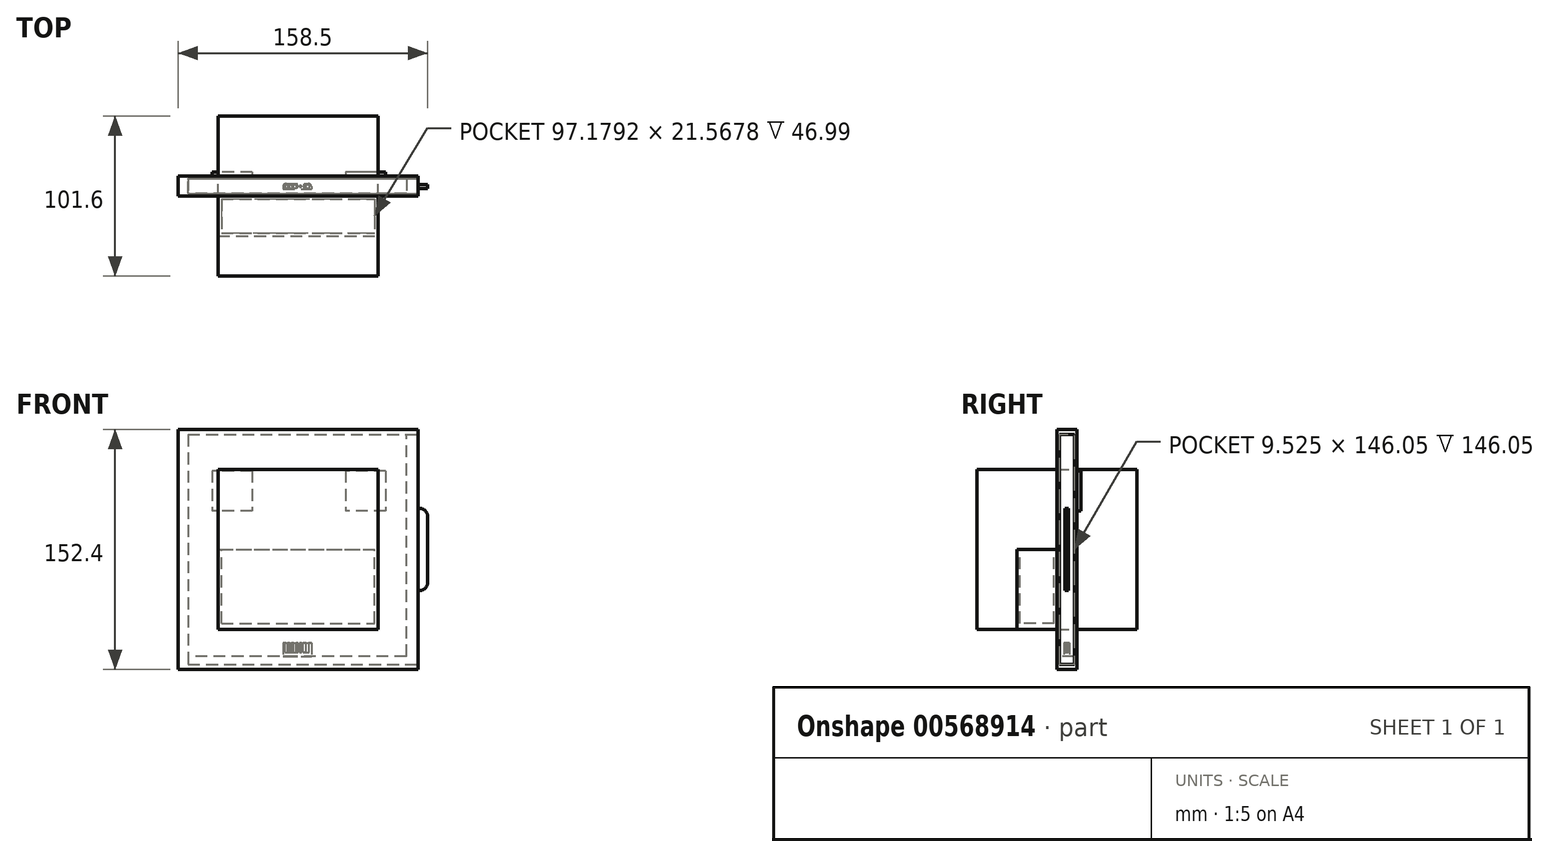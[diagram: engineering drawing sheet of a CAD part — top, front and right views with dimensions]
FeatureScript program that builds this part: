
annotation { "Feature Type Name" : "Feature", "Feature Type Description" : "" }
export const myFeature = defineFeature(function(context is Context, id is Id, definition is map)
    precondition{}
    {
        {
            var Q0;
            Q0=qCreatedBy(makeId("Front.planeOp"),FACE);
            var sketch = newSketch(context, id + "F0", { "sketchPlane" : qUnion([Q0])});
            skLineSegment(sketch, "E0.bottom", {"start": v(-34.8, 71.2) * mm, "end": v(34.8, 71.2) * mm});
            skLineSegment(sketch, "E0.top", {"start": v(-34.8, -71.2) * mm, "end": v(34.8, -71.2) * mm});
            skLineSegment(sketch, "E0.left", {"start": v(-34.8, 71.2) * mm, "end": v(-34.8, -71.2) * mm});
            skLineSegment(sketch, "E0.right", {"start": v(34.8, 71.2) * mm, "end": v(34.8, -71.2) * mm});
            skPoint(sketch, "E0.middle", {"position": v(0, 0) * mm});
            skSolve(sketch);
        }
        {
            var Q0;
            Q0=qCreatedBy(makeId("Front.planeOp"),FACE);
            var sketch = newSketch(context, id + "F1", { "sketchPlane" : qUnion([Q0])});
            skLineSegment(sketch, "E1.bottom", {"start": v(-76.2, 76.2) * mm, "end": v(76.2, 76.2) * mm});
            skLineSegment(sketch, "E1.top", {"start": v(-76.2, -76.2) * mm, "end": v(76.2, -76.2) * mm});
            skLineSegment(sketch, "E1.left", {"start": v(-76.2, 76.2) * mm, "end": v(-76.2, -76.2) * mm});
            skLineSegment(sketch, "E1.right", {"start": v(76.2, 76.2) * mm, "end": v(76.2, -76.2) * mm});
            skPoint(sketch, "E1.middle", {"position": v(0, 0) * mm});
            skSolve(sketch);
        }
        {
            var Q0;
            Q0=makeQuery(id+"F1.imprint","IMPRINT",FACE,{"disambiguationData":[TD([[makeQuery(id+"F1.imprint","IMPRINT",EDGE,{"derivedFrom":sQuery(id+"F1.wireOp",EDGE,"E1.bottom")}),-1.0]])]});
            extrude(context, id + "F2", {"entities" : qUnion([Q0]), "oppositeDirection" : true, "depth" : 12.7 * mm, "offsetDistance" : 25.4 * mm});
        }
        {
            var Q0;
            Q0=makeQuery(id+"F2.opExtrude","CAP_FACE",FACE,{"disambiguationData":[OSD([sQuery(id+"F1.wireOp",EDGE,"E1.bottom"),sQuery(id+"F1.wireOp",EDGE,"E1.top"),sQuery(id+"F1.wireOp",EDGE,"E1.left"),sQuery(id+"F1.wireOp",EDGE,"E1.right")])],"isStart":false});
            var sketch = newSketch(context, id + "F3", { "sketchPlane" : qUnion([Q0])});
            skLineSegment(sketch, "E2.bottom", {"start": v(-55.75, 49.94) * mm, "end": v(-30.35, 49.94) * mm});
            skLineSegment(sketch, "E2.top", {"start": v(-55.75, 24.54) * mm, "end": v(-30.35, 24.54) * mm});
            skLineSegment(sketch, "E2.left", {"start": v(-55.75, 49.94) * mm, "end": v(-55.75, 24.54) * mm});
            skLineSegment(sketch, "E2.right", {"start": v(-30.35, 49.94) * mm, "end": v(-30.35, 24.54) * mm});
            skPoint(sketch, "E2.middle", {"position": v(-43.05, 37.24) * mm});
            skLineSegment(sketch, "E3.bottom", {"start": v(29.1, 49.94) * mm, "end": v(54.5, 49.94) * mm});
            skLineSegment(sketch, "E3.top", {"start": v(29.1, 24.54) * mm, "end": v(54.5, 24.54) * mm});
            skLineSegment(sketch, "E3.left", {"start": v(29.1, 49.94) * mm, "end": v(29.1, 24.54) * mm});
            skLineSegment(sketch, "E3.right", {"start": v(54.5, 49.94) * mm, "end": v(54.5, 24.54) * mm});
            skPoint(sketch, "E3.middle", {"position": v(41.8, 37.24) * mm});
            skSolve(sketch);
        }
        {
            var Q0;
            Q0=makeQuery(id+"F3.imprint","IMPRINT",FACE,{"disambiguationData":[TD([[makeQuery(id+"F3.imprint","IMPRINT",EDGE,{"derivedFrom":sQuery(id+"F3.wireOp",EDGE,"E2.bottom")}),-1.0]])]});
            var Q1;
            Q1=makeQuery(id+"F3.imprint","IMPRINT",FACE,{"disambiguationData":[TD([[makeQuery(id+"F3.imprint","IMPRINT",EDGE,{"derivedFrom":sQuery(id+"F3.wireOp",EDGE,"E3.bottom")}),-1.0]])]});
            extrude(context, id + "F4", {"entities" : qUnion([Q0, Q1]), "operationType" : NewBodyOperationType.ADD, "depth" : 2.54 * mm, "offsetDistance" : 25.4 * mm});
        }
        {
            var Q0;
            Q0=makeQuery(id+"F2.opExtrude","SWEPT_FACE",FACE,{"disambiguationData":[OSD([sQuery(id+"F1.wireOp",EDGE,"E1.right")])]});
            var sketch = newSketch(context, id + "F5", { "sketchPlane" : qUnion([Q0])});
            skLineSegment(sketch, "E4.bottom", {"start": v(2.4, 71.2) * mm, "end": v(10.3, 71.2) * mm});
            skLineSegment(sketch, "E4.top", {"start": v(2.4, -71.2) * mm, "end": v(10.3, -71.2) * mm});
            skLineSegment(sketch, "E4.left", {"start": v(2.4, 71.2) * mm, "end": v(2.4, -71.2) * mm});
            skLineSegment(sketch, "E4.right", {"start": v(10.3, 71.2) * mm, "end": v(10.3, -71.2) * mm});
            skPoint(sketch, "E4.middle", {"position": v(6.35, 0) * mm});
            skPoint(sketch, "E4.middle.positionSnap0", {"position": v(12.7, 0) * mm});
            skPoint(sketch, "E4.centerSnap0", {"position": v(12.7, 0) * mm});
            skSolve(sketch);
        }
        {
            var Q0;
            Q0=makeQuery(id+"F5.imprint","IMPRINT",FACE,{"disambiguationData":[TD([[makeQuery(id+"F5.imprint","IMPRINT",EDGE,{"derivedFrom":sQuery(id+"F5.wireOp",EDGE,"E4.bottom")}),1.0]])]});
            var sketch = newSketch(context, id + "F6", { "sketchPlane" : qUnion([Q0])});
            skLineSegment(sketch, "E5.bottom", {"start": v(1.59, 73.03) * mm, "end": v(11.11, 73.03) * mm});
            skLineSegment(sketch, "E5.top", {"start": v(1.59, -73.03) * mm, "end": v(11.11, -73.03) * mm});
            skLineSegment(sketch, "E5.left", {"start": v(1.59, 73.03) * mm, "end": v(1.59, -73.03) * mm});
            skLineSegment(sketch, "E5.right", {"start": v(11.11, 73.03) * mm, "end": v(11.11, -73.03) * mm});
            skPoint(sketch, "E5.middle", {"position": v(6.35, 0) * mm});
            skSolve(sketch);
        }
        {
            var Q0;
            Q0=makeQuery(id+"F6.imprint","IMPRINT",FACE,{"disambiguationData":[TD([[makeQuery(id+"F6.imprint","IMPRINT",EDGE,{"derivedFrom":sQuery(id+"F6.wireOp",EDGE,"E5.bottom")}),-1.0]])]});
            var Q1;
            Q1=makeQuery(id+"F6.imprint","IMPRINT",FACE,{"disambiguationData":[TD([[makeQuery(id+"F6.imprint","IMPRINT",EDGE,{"derivedFrom":makeQuery(id+"F5.imprint","IMPRINT",EDGE,{"derivedFrom":sQuery(id+"F5.wireOp",EDGE,"E4.bottom")})}),-1.0]])]});
            extrude(context, id + "F7", {"entities" : qUnion([Q0, Q1]), "operationType" : NewBodyOperationType.REMOVE, "oppositeDirection" : true, "depth" : 146.05 * mm, "offsetDistance" : 25.4 * mm});
        }
        {
            var Q0;
            Q0=makeQuery(id+"F2.opExtrude","CAP_FACE",FACE,{"disambiguationData":[OSD([sQuery(id+"F1.wireOp",EDGE,"E1.bottom"),sQuery(id+"F1.wireOp",EDGE,"E1.top"),sQuery(id+"F1.wireOp",EDGE,"E1.left"),sQuery(id+"F1.wireOp",EDGE,"E1.right")])],"isStart":true});
            var sketch = newSketch(context, id + "F8", { "sketchPlane" : qUnion([Q0])});
            skLineSegment(sketch, "E6.bottom", {"start": v(-50.8, 50.8) * mm, "end": v(50.8, 50.8) * mm});
            skLineSegment(sketch, "E6.top", {"start": v(-50.8, -50.8) * mm, "end": v(50.8, -50.8) * mm});
            skLineSegment(sketch, "E6.left", {"start": v(-50.8, 50.8) * mm, "end": v(-50.8, -50.8) * mm});
            skLineSegment(sketch, "E6.right", {"start": v(50.8, 50.8) * mm, "end": v(50.8, -50.8) * mm});
            skPoint(sketch, "E6.middle", {"position": v(0, 0) * mm});
            skLineSegment(sketch, "E7", {"start": v(-50.8, 0) * mm, "end": v(50.8, 0) * mm});
            skSolve(sketch);
        }
        {
            var Q0;
            {var subQ0=sQuery(id+"F8.wireOp",EDGE,"E6.top");Q0=makeQuery(id+"F8.imprint","IMPRINT",FACE,{"disambiguationData":[TD([[makeQuery(id+"F8.imprint","IMPRINT",EDGE,{"derivedFrom":subQ0}),1.0]])]});}
            extrude(context, id + "F9", {"entities" : qUnion([Q0]), "operationType" : NewBodyOperationType.ADD, "depth" : 25.4 * mm, "offsetDistance" : 25.4 * mm});
        }
        {
            var Q0;
            Q0=makeQuery(id+"F9.opExtrude","SWEPT_FACE",FACE,{"disambiguationData":[OSD([sQuery(id+"F8.wireOp",EDGE,"E7")])]});
            var sketch = newSketch(context, id + "F10", { "sketchPlane" : qUnion([Q0])});
            skLineSegment(sketch, "E8.bottom", {"start": v(-48.59, -1.92) * mm, "end": v(48.59, -1.92) * mm});
            skLineSegment(sketch, "E8.top", {"start": v(-48.59, -23.48) * mm, "end": v(48.59, -23.48) * mm});
            skLineSegment(sketch, "E8.left", {"start": v(-48.59, -1.92) * mm, "end": v(-48.59, -23.48) * mm});
            skLineSegment(sketch, "E8.right", {"start": v(48.59, -1.92) * mm, "end": v(48.59, -23.48) * mm});
            skPoint(sketch, "E8.middle", {"position": v(0, -12.7) * mm});
            skPoint(sketch, "E8.middle.positionSnap0", {"position": v(0, -25.4) * mm});
            skPoint(sketch, "E8.centerSnap0", {"position": v(0, -25.4) * mm});
            skSolve(sketch);
        }
        {
            var Q0;
            Q0=makeQuery(id+"F10.imprint","IMPRINT",FACE,{"disambiguationData":[TD([[makeQuery(id+"F10.imprint","IMPRINT",EDGE,{"derivedFrom":sQuery(id+"F10.wireOp",EDGE,"E8.bottom")}),-1.0]])]});
            extrude(context, id + "F11", {"entities" : qUnion([Q0]), "operationType" : NewBodyOperationType.REMOVE, "oppositeDirection" : true, "depth" : 47 * mm, "offsetDistance" : 25.4 * mm});
        }
        {
            var Q0;
            Q0=makeQuery(id+"F6.imprint","IMPRINT",FACE,{"disambiguationData":[TD([[makeQuery(id+"F6.imprint","IMPRINT",EDGE,{"derivedFrom":sQuery(id+"F6.wireOp",EDGE,"E5.bottom")}),-1.0]])]});
            var Q1;
            Q1=makeQuery(id+"F6.imprint","IMPRINT",FACE,{"disambiguationData":[TD([[makeQuery(id+"F6.imprint","IMPRINT",EDGE,{"derivedFrom":makeQuery(id+"F5.imprint","IMPRINT",EDGE,{"derivedFrom":sQuery(id+"F5.wireOp",EDGE,"E4.bottom")})}),-1.0]])]});
            extrude(context, id + "F12", {"entities" : qUnion([Q0, Q1]), "oppositeDirection" : true, "depth" : 146.05 * mm, "offsetDistance" : 25.4 * mm});
        }
        {
            var Q0;
            Q0=makeQuery(id+"F12.opExtrude","SWEPT_FACE",FACE,{"disambiguationData":[OSD([sQuery(id+"F6.wireOp",EDGE,"E5.left")])]});
            var sketch = newSketch(context, id + "F13", { "sketchPlane" : qUnion([Q0])});
            skLineSegment(sketch, "E9.bottom", {"start": v(68.8, -67.84) * mm, "end": v(-208.5, -67.84) * mm});
            skLineSegment(sketch, "E9.top", {"start": v(68.8, 213.9) * mm, "end": v(-208.5, 213.9) * mm});
            skLineSegment(sketch, "E9.left", {"start": v(68.8, -67.84) * mm, "end": v(68.8, 213.9) * mm});
            skLineSegment(sketch, "E9.right", {"start": v(-208.5, -67.84) * mm, "end": v(-208.5, 213.9) * mm});
            skPoint(sketch, "E9.middle", {"position": v(-69.85, 73.03) * mm});
            skSolve(sketch);
        }
        {
            var Q0;
            {var subQ0=sQuery(id+"F13.wireOp",EDGE,"E9.left");var subQ1=sQuery(id+"F13.wireOp",EDGE,"E9.bottom");var subQ2=makeQuery(id+"F13.imprint","INTERSECT",VERTEX,{"derivedFrom":[subQ1,subQ0]});Q0=makeQuery(id+"F13.imprint","IMPRINT",FACE,{"disambiguationData":[TD([[makeQuery(id+"F13.imprint","IMPRINT",EDGE,{"disambiguationData":[TD([[subQ2,-1.0]])],"derivedFrom":subQ1}),-1.0]])]});}
            extrude(context, id + "F14", {"entities" : qUnion([Q0]), "operationType" : NewBodyOperationType.REMOVE, "oppositeDirection" : true, "depth" : 9.25 * mm, "offsetDistance" : 25.4 * mm});
        }
        {
            var Q0;
            Q0=makeQuery(id+"F14.boolean.opBoolean","COPY",FACE,{"derivedFrom":makeQuery(id+"F14.opExtrude","SWEPT_FACE",FACE,{"disambiguationData":[OSD([sQuery(id+"F13.wireOp",EDGE,"E9.bottom")])]})});
            var sketch = newSketch(context, id + "F15", { "sketchPlane" : qUnion([Q0])});
            skLineSegment(sketch, "E10.bottom", {"start": v(-7.65, 7.85) * mm, "end": v(6.6, 7.85) * mm});
            skLineSegment(sketch, "E10.top", {"start": v(-9.55, 4.47) * mm, "end": v(8.5, 4.47) * mm});
            skLineSegment(sketch, "E10.left", {"start": v(-9.55, 5.94) * mm, "end": v(-9.55, 4.47) * mm});
            skLineSegment(sketch, "E10.right", {"start": v(8.5, 5.94) * mm, "end": v(8.5, 4.47) * mm});
            skPoint(sketch, "E10.middle", {"position": v(-0.52, 6.16) * mm});
            skPoint(sketch, "E11.visualSharp", {"position": v(-9.55, 7.85) * mm});
            skArc(sketch, "E11.filletArc", {"start": v(-7.65, 7.85) * mm, "mid": v(-9, 7.29) * mm, "end": v(-9.55, 5.94) * mm});
            skPoint(sketch, "E12.visualSharp", {"position": v(8.5, 7.85) * mm});
            skArc(sketch, "E12.filletArc", {"start": v(8.5, 5.94) * mm, "mid": v(7.95, 7.29) * mm, "end": v(6.6, 7.85) * mm});
            skSolve(sketch);
        }
        {
            var Q0;
            Q0=makeQuery(id+"F15.imprint","IMPRINT",FACE,{"disambiguationData":[TD([[makeQuery(id+"F15.imprint","IMPRINT",EDGE,{"derivedFrom":sQuery(id+"F15.wireOp",EDGE,"E10.bottom")}),-1.0]])]});
            extrude(context, id + "F16", {"entities" : qUnion([Q0]), "operationType" : NewBodyOperationType.ADD, "depth" : 8.6 * mm, "offsetDistance" : 25.4 * mm});
        }
        {
            var Q0;
            Q0=makeQuery(id+"F16.opExtrude","CAP_FACE",FACE,{"disambiguationData":[OSD([sQuery(id+"F15.wireOp",EDGE,"E10.bottom"),sQuery(id+"F15.wireOp",EDGE,"E10.top"),sQuery(id+"F15.wireOp",EDGE,"E10.left"),sQuery(id+"F15.wireOp",EDGE,"E10.right"),sQuery(id+"F15.wireOp",EDGE,"E11.filletArc"),sQuery(id+"F15.wireOp",EDGE,"E12.filletArc")])],"isStart":false});
            var sketch = newSketch(context, id + "F17", { "sketchPlane" : qUnion([Q0])});
            skLineSegment(sketch, "E13.bottom", {"start": v(-8.26, 7.4) * mm, "end": v(7.02, 7.4) * mm});
            skLineSegment(sketch, "E13.top", {"start": v(-8.26, 4.94) * mm, "end": v(7.02, 4.94) * mm});
            skLineSegment(sketch, "E13.left", {"start": v(-8.26, 7.4) * mm, "end": v(-8.26, 4.94) * mm});
            skLineSegment(sketch, "E13.right", {"start": v(7.02, 7.4) * mm, "end": v(7.02, 4.94) * mm});
            skPoint(sketch, "E13.middle", {"position": v(-0.62, 6.16) * mm});
            skCircle(sketch, "E14", {"center": v(-5.9, 6.27) * mm, "radius": 0.68 * mm});
            skCircle(sketch, "E15", {"center": v(-0.62, 6.16) * mm, "radius": 0.68 * mm});
            skCircle(sketch, "E16", {"center": v(4.21, 6.16) * mm, "radius": 0.87 * mm});
            skCircle(sketch, "E17", {"center": v(1.6, 6.16) * mm, "radius": 0.6 * mm});
            skCircle(sketch, "E18", {"center": v(-3.4, 6.16) * mm, "radius": 0.6 * mm});
            skSolve(sketch);
        }
        {
            var Q0;
            Q0=makeQuery(id+"F17.imprint","IMPRINT",FACE,{"disambiguationData":[TD([[makeQuery(id+"F17.imprint","IMPRINT",EDGE,{"derivedFrom":sQuery(id+"F17.wireOp",EDGE,"E13.bottom")}),-1.0]])]});
            extrude(context, id + "F18", {"entities" : qUnion([Q0]), "operationType" : NewBodyOperationType.REMOVE, "oppositeDirection" : true, "depth" : 6.07 * mm, "offsetDistance" : 25.4 * mm});
        }
        {
            var Q0;
            Q0=makeQuery(id+"F12.opExtrude","CAP_FACE",FACE,{"disambiguationData":[OSD([sQuery(id+"F6.wireOp",EDGE,"E5.bottom"),sQuery(id+"F6.wireOp",EDGE,"E5.top"),sQuery(id+"F6.wireOp",EDGE,"E5.left"),sQuery(id+"F6.wireOp",EDGE,"E5.right")])],"isStart":true});
            var sketch = newSketch(context, id + "F19", { "sketchPlane" : qUnion([Q0])});
            skLineSegment(sketch, "E19.bottom", {"start": v(4.85, 26.15) * mm, "end": v(7.32, 26.15) * mm});
            skLineSegment(sketch, "E19.top", {"start": v(4.85, -26.15) * mm, "end": v(7.32, -26.15) * mm});
            skLineSegment(sketch, "E19.left", {"start": v(4.85, 26.15) * mm, "end": v(4.85, -26.15) * mm});
            skLineSegment(sketch, "E19.right", {"start": v(7.32, 26.15) * mm, "end": v(7.32, -26.15) * mm});
            skPoint(sketch, "E19.middle", {"position": v(6.09, 0) * mm});
            skSolve(sketch);
        }
        {
            var Q0;
            Q0=makeQuery(id+"F19.imprint","IMPRINT",FACE,{"disambiguationData":[TD([[makeQuery(id+"F19.imprint","IMPRINT",EDGE,{"derivedFrom":sQuery(id+"F19.wireOp",EDGE,"E19.bottom")}),-1.0]])]});
            extrude(context, id + "F20", {"entities" : qUnion([Q0]), "operationType" : NewBodyOperationType.ADD, "depth" : 6.1 * mm, "offsetDistance" : 25.4 * mm});
        }
        {
            var Q0;
            Q0=makeQuery(id+"F20.opExtrude","CAP_EDGE",EDGE,{"disambiguationData":[OSD([sQuery(id+"F19.wireOp",EDGE,"E19.bottom")])],"isStart":false});
            var Q1;
            Q1=makeQuery(id+"F20.opExtrude","CAP_EDGE",EDGE,{"disambiguationData":[OSD([sQuery(id+"F19.wireOp",EDGE,"E19.top")])],"isStart":false});
            fillet(context, id + "F21", {"entities" : qUnion([Q0, Q1]), "radius" : 5.08 * mm, "tangentPropagation" : true, "allowEdgeOverflow" : false});
        }
        {
            var Q0;
            Q0=qCreatedBy(makeId("Front.planeOp"),FACE);
            var sketch = newSketch(context, id + "F22", { "sketchPlane" : qUnion([Q0])});
            skLineSegment(sketch, "E20.bottom", {"start": v(-50.8, 50.8) * mm, "end": v(50.8, 50.8) * mm});
            skLineSegment(sketch, "E20.top", {"start": v(-50.8, -50.8) * mm, "end": v(50.8, -50.8) * mm});
            skLineSegment(sketch, "E20.left", {"start": v(-50.8, 50.8) * mm, "end": v(-50.8, -50.8) * mm});
            skLineSegment(sketch, "E20.right", {"start": v(50.8, 50.8) * mm, "end": v(50.8, -50.8) * mm});
            skPoint(sketch, "E20.middle", {"position": v(0, 0) * mm});
            skSolve(sketch);
        }
        {
            var Q0;
            Q0 = qSketchRegion(id + "F22", true);
            extrude(context, id + "F23", {"entities" : qUnion([Q0]), "endBound" : BoundingType.SYMMETRIC, "depth" : 101.6 * mm, "offsetDistance" : 25.4 * mm});
        }
    });
